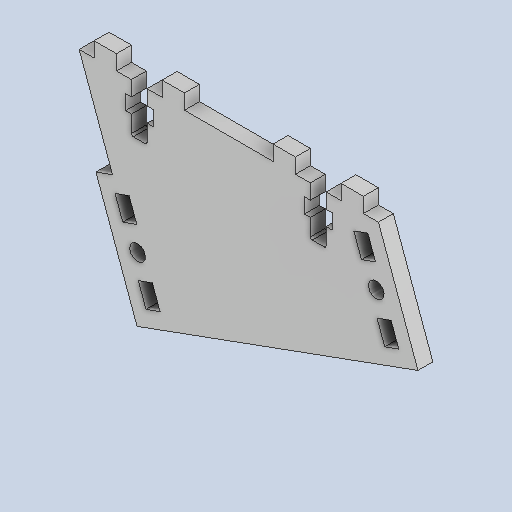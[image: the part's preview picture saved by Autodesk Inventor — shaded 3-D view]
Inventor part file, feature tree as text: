
AUTODESK INVENTOR PART (.ipt)
format: ipt  version: 2024.1 (Build 281209000, 209)  size: 374,272 bytes
history: native  units: mm
features: other x8, extrude x1, sketch x1
ambient origin geometry x8: Origin, YZ Plane, XZ Plane, XY Plane, X Axis, Y Axis, Z Axis, Center Point
bodies: Solide1 (feature_tree)
feature tree (10):
  other  "shared_parameters.ipt"
  other  "Blocs"
  extrude  "Extrusion1"  Depth=10.0mm
  other  "Anchor (screw side)"
  other  "Anchor (nut side)"
  sketch  "Esquisse1"
  other  "Anchor (screw side):2"
  other  "Anchor (screw side):3"
  other  "Anchor (nut side):1"
  other  "Anchor (nut side):2"
